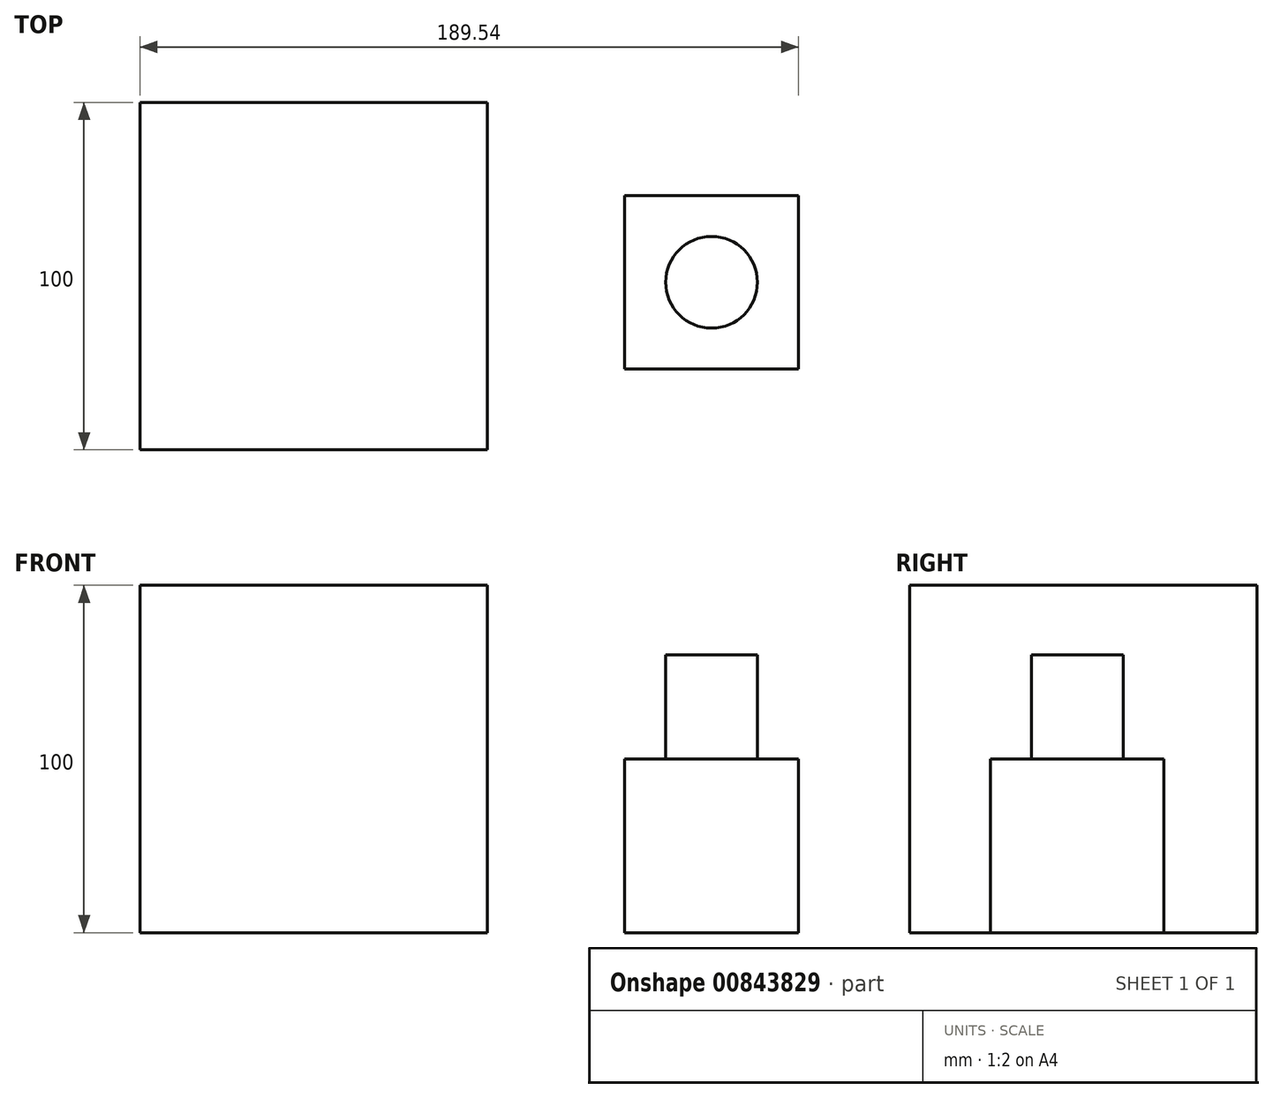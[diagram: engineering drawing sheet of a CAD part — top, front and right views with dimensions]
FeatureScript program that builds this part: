
annotation { "Feature Type Name" : "Feature", "Feature Type Description" : "" }
export const myFeature = defineFeature(function(context is Context, id is Id, definition is map)
    precondition{}
    {
        {
            var Q0;
            Q0=qCreatedBy(makeId("Top.planeOp"),FACE);
            var sketch = newSketch(context, id + "F0", { "sketchPlane" : qUnion([Q0])});
            skLineSegment(sketch, "E0.bottom", {"start": v(-63.5, 45.38) * mm, "end": v(36.5, 45.38) * mm});
            skLineSegment(sketch, "E0.top", {"start": v(-63.5, -54.62) * mm, "end": v(36.5, -54.62) * mm});
            skLineSegment(sketch, "E0.left", {"start": v(-63.5, 45.38) * mm, "end": v(-63.5, -54.62) * mm});
            skLineSegment(sketch, "E0.right", {"start": v(36.5, 45.38) * mm, "end": v(36.5, -54.62) * mm});
            skSolve(sketch);
        }
        {
            var Q0;
            Q0=makeQuery(id+"F0.imprint","IMPRINT",FACE,{"disambiguationData":[TD([[makeQuery(id+"F0.imprint","IMPRINT",EDGE,{"derivedFrom":sQuery(id+"F0.wireOp",EDGE,"E0.bottom")}),-1.0]])]});
            extrude(context, id + "F1", {"entities" : qUnion([Q0]), "depth" : 100 * mm, "offsetDistance" : 25 * mm});
        }
        {
            var Q0;
            Q0=qCreatedBy(makeId("Top.planeOp"),FACE);
            var sketch = newSketch(context, id + "F2", { "sketchPlane" : qUnion([Q0])});
            skLineSegment(sketch, "E1.bottom", {"start": v(76.05, 18.6) * mm, "end": v(126.05, 18.6) * mm});
            skLineSegment(sketch, "E1.top", {"start": v(76.05, -31.4) * mm, "end": v(126.05, -31.4) * mm});
            skLineSegment(sketch, "E1.left", {"start": v(76.05, 18.6) * mm, "end": v(76.05, -31.4) * mm});
            skLineSegment(sketch, "E1.right", {"start": v(126.05, 18.6) * mm, "end": v(126.05, -31.4) * mm});
            skSolve(sketch);
        }
        {
            var Q0;
            Q0=makeQuery(id+"F2.imprint","IMPRINT",FACE,{"disambiguationData":[TD([[makeQuery(id+"F2.imprint","IMPRINT",EDGE,{"derivedFrom":sQuery(id+"F2.wireOp",EDGE,"E1.bottom")}),-1.0]])]});
            extrude(context, id + "F3", {"entities" : qUnion([Q0]), "depth" : 50 * mm, "offsetDistance" : 25 * mm});
        }
        {
            var Q0;
            Q0=makeQuery(id+"F3.opExtrude","CAP_FACE",FACE,{"disambiguationData":[OSD([sQuery(id+"F2.wireOp",EDGE,"E1.bottom"),sQuery(id+"F2.wireOp",EDGE,"E1.top"),sQuery(id+"F2.wireOp",EDGE,"E1.left"),sQuery(id+"F2.wireOp",EDGE,"E1.right")])],"isStart":false});
            var sketch = newSketch(context, id + "F4", { "sketchPlane" : qUnion([Q0])});
            skCircle(sketch, "E2", {"center": v(101.05, -6.4) * mm, "radius": 13.2 * mm});
            skSolve(sketch);
        }
        {
            var Q0;
            Q0=makeQuery(id+"F4.imprint","IMPRINT",FACE,{"disambiguationData":[TD([[makeQuery(id+"F4.imprint","IMPRINT",EDGE,{"derivedFrom":sQuery(id+"F4.wireOp",EDGE,"E2")}),1.0]])]});
            extrude(context, id + "F5", {"entities" : qUnion([Q0]), "operationType" : NewBodyOperationType.ADD, "depth" : 30 * mm, "offsetDistance" : 25 * mm});
        }
    });
